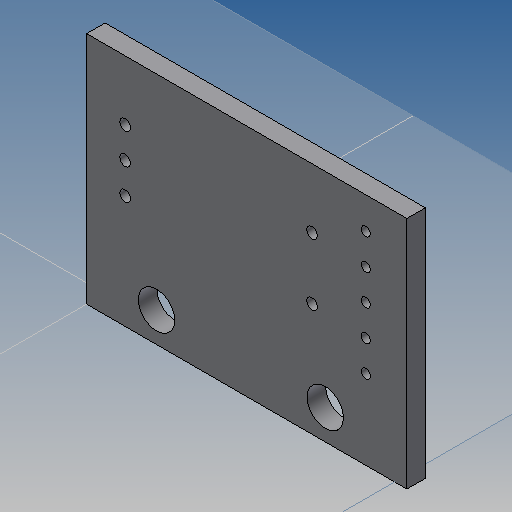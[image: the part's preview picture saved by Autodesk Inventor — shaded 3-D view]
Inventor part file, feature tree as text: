
AUTODESK INVENTOR PART (.ipt)
format: ipt  version: 2019 (Build 230136000, 136)  size: 137,728 bytes
history: native  units: in
note: dims shown in document units (in); Inventor stores cm internally (conversion verified against a paired STEP export)
features: reference x3, sketch x2, extrude x1, hole x1
ambient origin geometry x8: Origin, YZ Plane, XZ Plane, XY Plane, X Axis, Y Axis, Z Axis, Center Point
bodies: Solid1 (feature_tree)
feature tree (7):
  extrude  "Extrusion1"  Depth=0.761in
  hole  "Hole1"  [1 undecoded]
  sketch  "Sketch1"  dims[d0=1.04in d1=0.761in]
  sketch  "Sketch3"  dims[d2=0.1181in d3=0.1181in d4=0.227in d5=0.097in d6=0.548in d7=0.265in d8=0.095in d9=0.5in d10=0.208in d11=0.086in d12=0.05in d14=0.1in d15=0.1in d16=0.1in d18=0.0475in d19=0.1in d20=0.03in d21=0.03in d22=0.03in d23=0.03in d24=0.03in d25=0.035in d26=0.035in d27=0.035in d28=0.194in d29=0.1in d30=0.1in d31=0.125in d32=0.06in d33=0.0in d41=0.035in d42=0.75in d43=0.375in d44=0.25in d45=0.5635in d46=1.0in d47=0.8108in]
  reference  "Reference1"
  reference  "Reference2"
  reference  "Reference3"
note: 1 required parameter value undecoded (feature->parameter linkage not recoverable at this tier; creation-order binding heuristic only, values carry confidence <= 0.55)
